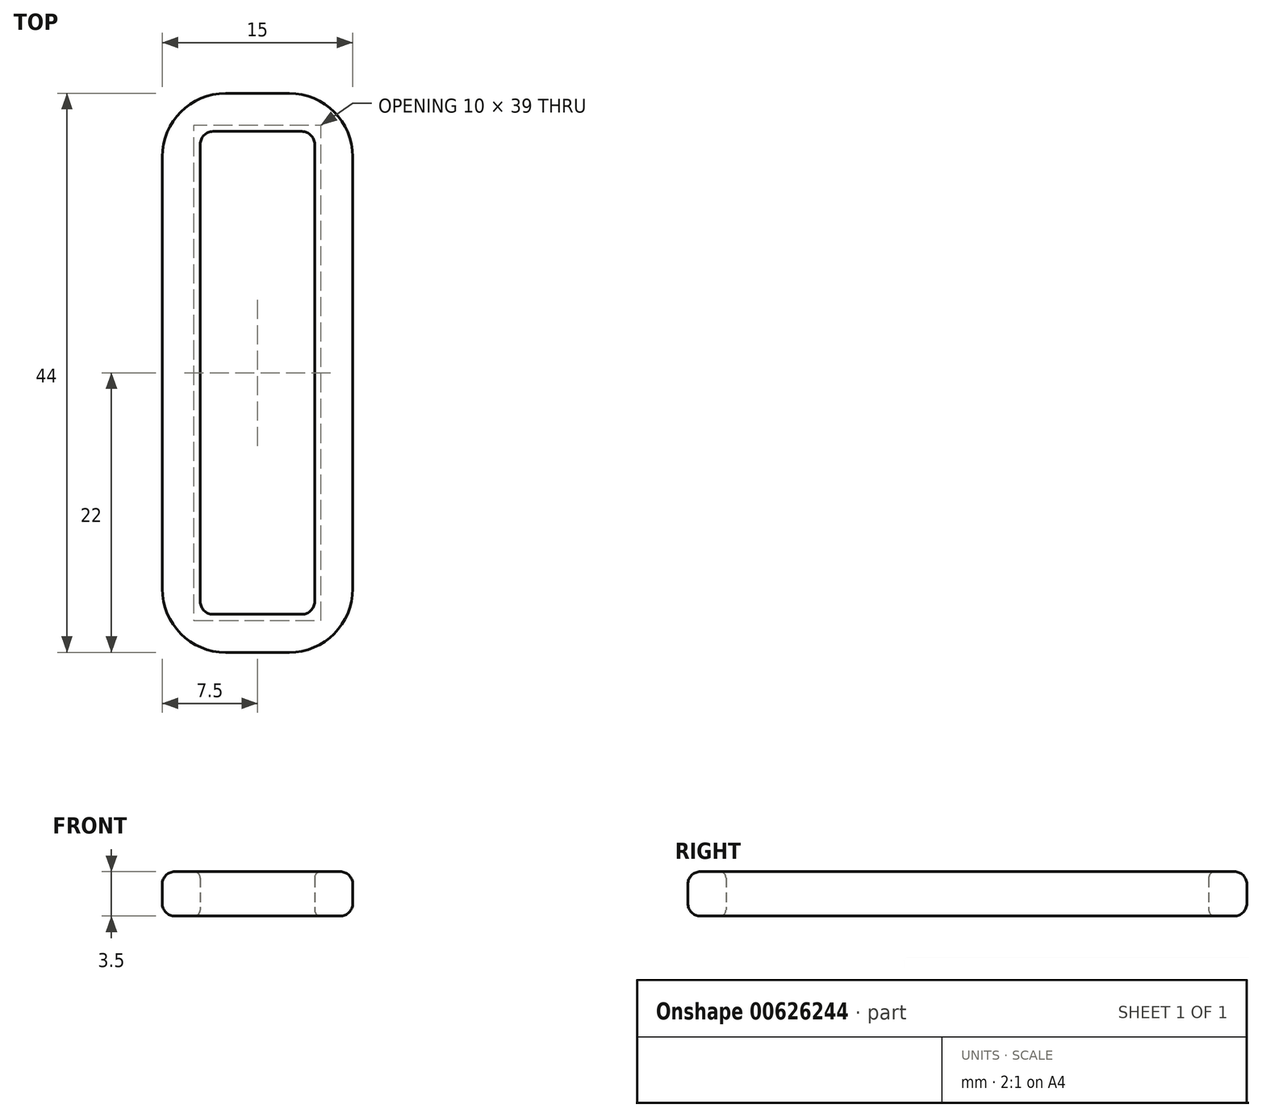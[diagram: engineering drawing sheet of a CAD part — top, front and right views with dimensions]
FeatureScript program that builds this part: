
annotation { "Feature Type Name" : "Feature", "Feature Type Description" : "" }
export const myFeature = defineFeature(function(context is Context, id is Id, definition is map)
    precondition{}
    {
        {
            var Q0;
            Q0=qCreatedBy(makeId("Top.planeOp"),FACE);
            var sketch = newSketch(context, id + "F0", { "sketchPlane" : qUnion([Q0])});
            skLineSegment(sketch, "E0.bottom", {"start": v(-4.5, 19) * mm, "end": v(4.5, 19) * mm});
            skLineSegment(sketch, "E0.top", {"start": v(-4.5, -19) * mm, "end": v(4.5, -19) * mm});
            skLineSegment(sketch, "E0.left", {"start": v(-4.5, 19) * mm, "end": v(-4.5, -19) * mm});
            skLineSegment(sketch, "E0.right", {"start": v(4.5, 19) * mm, "end": v(4.5, -19) * mm});
            skLineSegment(sketch, "E1.bottom", {"start": v(-7.5, 22) * mm, "end": v(7.5, 22) * mm});
            skLineSegment(sketch, "E1.top", {"start": v(-7.5, -22) * mm, "end": v(7.5, -22) * mm});
            skLineSegment(sketch, "E1.left", {"start": v(-7.5, 22) * mm, "end": v(-7.5, -22) * mm});
            skLineSegment(sketch, "E1.right", {"start": v(7.5, 22) * mm, "end": v(7.5, -22) * mm});
            skLineSegment(sketch, "E2", {"start": v(-4.5, 0) * mm, "end": v(4.5, 0) * mm, "construction": true});
            skPoint(sketch, "E3", {"position": v(0, 0) * mm});
            skSolve(sketch);
        }
        {
            var Q0;
            Q0 = qSketchRegion(id + "F0", true);
            extrude(context, id + "F1", {"entities" : qUnion([Q0]), "depth" : 3.5 * mm, "offsetDistance" : 25 * mm});
        }
        {
            var Q0;
            Q0=makeQuery(id+"F1.opExtrude","SWEPT_EDGE",EDGE,{"disambiguationData":[OSD([sQuery(id+"F0.wireOp",EDGE,"E0.bottom"),sQuery(id+"F0.wireOp",EDGE,"E0.right")])]});
            var Q1;
            Q1=makeQuery(id+"F1.opExtrude","SWEPT_EDGE",EDGE,{"disambiguationData":[OSD([sQuery(id+"F0.wireOp",EDGE,"E0.bottom"),sQuery(id+"F0.wireOp",EDGE,"E0.left")])]});
            var Q2;
            Q2=makeQuery(id+"F1.opExtrude","SWEPT_EDGE",EDGE,{"disambiguationData":[OSD([sQuery(id+"F0.wireOp",EDGE,"E0.top"),sQuery(id+"F0.wireOp",EDGE,"E0.left")])]});
            var Q3;
            Q3=makeQuery(id+"F1.opExtrude","SWEPT_EDGE",EDGE,{"disambiguationData":[OSD([sQuery(id+"F0.wireOp",EDGE,"E0.top"),sQuery(id+"F0.wireOp",EDGE,"E0.right")])]});
            fillet(context, id + "F2", {"entities" : qUnion([Q0, Q1, Q2, Q3]), "radius" : 1 * mm, "tangentPropagation" : true, "allowEdgeOverflow" : false});
        }
        {
            var Q0;
            Q0=makeQuery(id+"F1.opExtrude","SWEPT_EDGE",EDGE,{"disambiguationData":[OSD([sQuery(id+"F0.wireOp",EDGE,"E1.top"),sQuery(id+"F0.wireOp",EDGE,"E1.left")])]});
            var Q1;
            Q1=makeQuery(id+"F1.opExtrude","SWEPT_EDGE",EDGE,{"disambiguationData":[OSD([sQuery(id+"F0.wireOp",EDGE,"E1.top"),sQuery(id+"F0.wireOp",EDGE,"E1.right")])]});
            var Q2;
            Q2=makeQuery(id+"F1.opExtrude","SWEPT_EDGE",EDGE,{"disambiguationData":[OSD([sQuery(id+"F0.wireOp",EDGE,"E1.bottom"),sQuery(id+"F0.wireOp",EDGE,"E1.left")])]});
            var Q3;
            Q3=makeQuery(id+"F1.opExtrude","SWEPT_EDGE",EDGE,{"disambiguationData":[OSD([sQuery(id+"F0.wireOp",EDGE,"E1.bottom"),sQuery(id+"F0.wireOp",EDGE,"E1.right")])]});
            fillet(context, id + "F3", {"entities" : qUnion([Q0, Q1, Q2, Q3]), "radius" : 5 * mm, "tangentPropagation" : true, "allowEdgeOverflow" : false});
        }
        {
            var Q0;
            Q0=makeQuery(id+"F1.opExtrude","CAP_EDGE",EDGE,{"disambiguationData":[OSD([sQuery(id+"F0.wireOp",EDGE,"E0.bottom")])],"isStart":true});
            var Q1;
            Q1=makeQuery(id+"F1.opExtrude","CAP_EDGE",EDGE,{"disambiguationData":[OSD([sQuery(id+"F0.wireOp",EDGE,"E0.bottom")])],"isStart":false});
            fillet(context, id + "F4", {"entities" : qUnion([Q0, Q1]), "radius" : .5 * mm, "tangentPropagation" : true, "allowEdgeOverflow" : false});
        }
        {
            var Q0;
            Q0=makeQuery(id+"F1.opExtrude","CAP_EDGE",EDGE,{"disambiguationData":[OSD([sQuery(id+"F0.wireOp",EDGE,"E1.top")])],"isStart":false});
            var Q1;
            Q1=makeQuery(id+"F1.opExtrude","CAP_EDGE",EDGE,{"disambiguationData":[OSD([sQuery(id+"F0.wireOp",EDGE,"E1.top")])],"isStart":true});
            fillet(context, id + "F5", {"entities" : qUnion([Q0, Q1]), "radius" : 1 * mm, "tangentPropagation" : true, "allowEdgeOverflow" : false});
        }
    });
